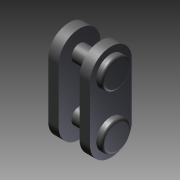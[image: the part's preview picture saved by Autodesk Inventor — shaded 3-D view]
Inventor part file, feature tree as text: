
AUTODESK INVENTOR PART (.ipt)
format: ipt  version: 2011 SP1 (Build 150282100, 282)  size: 161,280 bytes
history: native  units: mm
features: other x14, sketch x5, extrude x3, revolve x2
ambient origin geometry x8: Origin, YZ Plane, XZ Plane, XY Plane, X Axis, Y Axis, Z Axis, Center Point
bodies: Solid1 (feature_tree)
feature tree (24):
  extrude  "Extrusion1"  TaperAngle=360.0deg  [1 undecoded]
  revolve  "Revolution1"  [1 undecoded]
  revolve  "Revolution2"  [1 undecoded]
  extrude  "Extrusion2"  [1 undecoded]
  extrude  "Extrusion3"  [1 undecoded]
  other  "ZS1_XY"
  other  "ZS1_YZ"
  other  "ZS1_ZX"
  other  "ZS1_X"
  other  "ZS1_Y"
  other  "ZS1_Z"
  other  "ZS1_Center"
  other  "ZS2_XY"
  other  "ZS2_YZ"
  other  "ZS2_ZX"
  other  "ZS2_X"
  other  "ZS2_Y"
  other  "ZS2_Z"
  other  "ZS2_Center"
  sketch  "Skizze_1"  dims[d0=8.0mm d1=0.0mm d2=360.0deg]
  sketch  "Skizze_2"  dims[d3=360.0deg d4=8.0mm d5=0.0mm]
  sketch  "Skizze_3"  dims[d6=20.0mm d7=0.0mm]
  sketch  "Skizze_4"
  sketch  "Skizze_5"
note: 5 required parameter values undecoded (feature->parameter linkage not recoverable at this tier; creation-order binding heuristic only, values carry confidence <= 0.55)